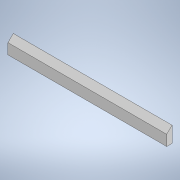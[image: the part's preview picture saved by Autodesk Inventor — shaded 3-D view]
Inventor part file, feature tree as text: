
AUTODESK INVENTOR PART (.ipt)
format: ipt  version: 2020 (Build 240168000, 168)  size: 96,256 bytes
history: native  units: mm
features: extrude x1, chamfer x1, sketch x1
ambient origin geometry x8: Origin, YZ Plane, XZ Plane, XY Plane, X Axis, Y Axis, Z Axis, Center Point
bodies: Solid1 (feature_tree)
feature tree (3):
  extrude  "Extrusion1"  Depth=10.0mm
  chamfer  "Chamfer1"  Distance=10.0mm
  sketch  "Sketch1"  dims[d0=300.0mm d1=30.0mm d2=10.0mm d3=0.0mm d4=10.0mm d5=2.0mm d6=45.0deg]
